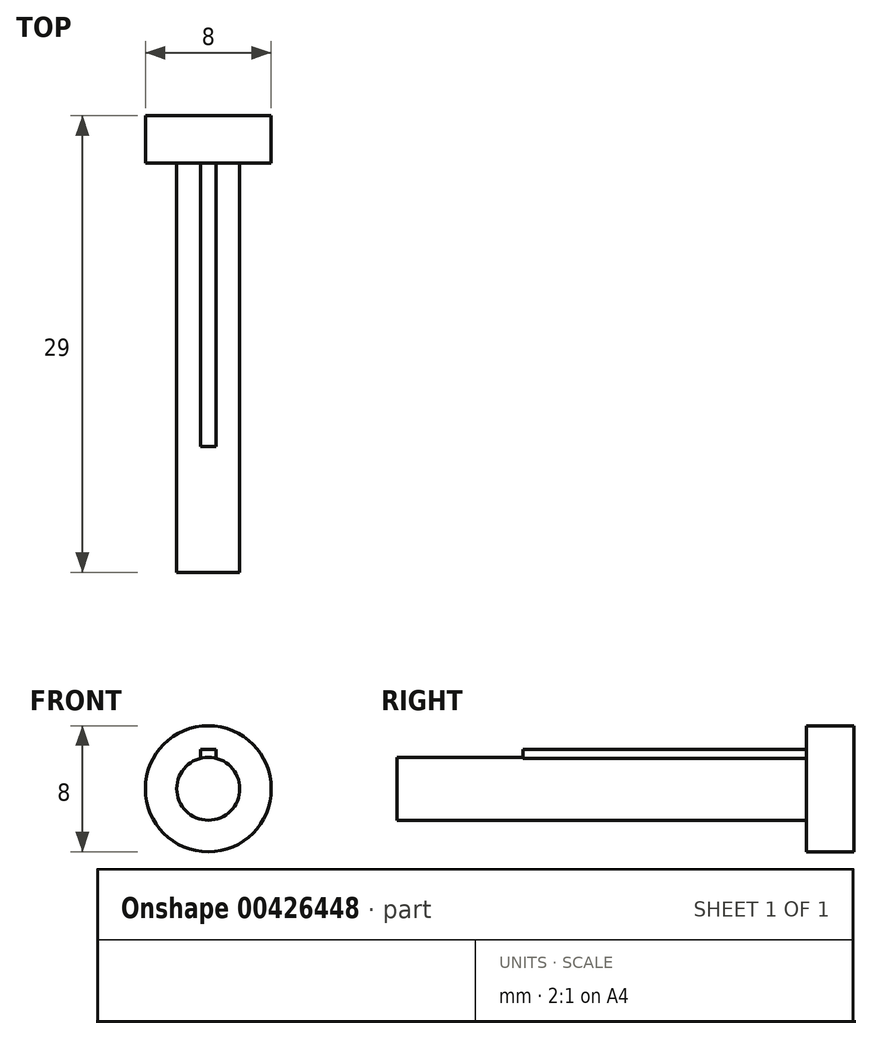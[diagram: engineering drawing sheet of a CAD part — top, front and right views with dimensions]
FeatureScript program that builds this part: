
annotation { "Feature Type Name" : "Feature", "Feature Type Description" : "" }
export const myFeature = defineFeature(function(context is Context, id is Id, definition is map)
    precondition{}
    {
        {
            var Q0;
            Q0=qCreatedBy(makeId("Right.planeOp"),FACE);
            var sketch = newSketch(context, id + "F0", { "sketchPlane" : qUnion([Q0])});
            skLineSegment(sketch, "E0", {"start": v(23.19, 0) * mm, "end": v(23.19, 4) * mm});
            skLineSegment(sketch, "E1", {"start": v(23.19, 4) * mm, "end": v(20.19, 4) * mm});
            skLineSegment(sketch, "E2", {"start": v(20.19, 4) * mm, "end": v(20.19, 2) * mm});
            skLineSegment(sketch, "E3", {"start": v(20.19, 2) * mm, "end": v(-5.81, 2) * mm});
            skLineSegment(sketch, "E4", {"start": v(-5.81, 2) * mm, "end": v(-5.81, 0) * mm});
            skLineSegment(sketch, "E5", {"start": v(-5.81, 0) * mm, "end": v(23.19, 0) * mm});
            skLineSegment(sketch, "E6", {"start": v(-13.83, 0) * mm, "end": v(22.3, 0) * mm, "construction": true});
            skSolve(sketch);
        }
        {
            var Q0;
            Q0 = qSketchRegion(id + "F0", true);
            var Q1;
            Q1=sQuery(id+"F0.wireOp",EDGE,"E6");
            revolve(context, id + "F1", {"entities" : qUnion([Q0]), "axis" : qUnion([Q1]), "revolveType" : RevolveType.FULL});
        }
        {
            var Q0;
            Q0=makeQuery(id+"F1.opRevolve","SWEPT_FACE",FACE,{"disambiguationData":[OSD([sQuery(id+"F0.wireOp",EDGE,"E2")])]});
            var sketch = newSketch(context, id + "F2", { "sketchPlane" : qUnion([Q0])});
            skLineSegment(sketch, "E7.bottom", {"start": v(-0.5, 2.5) * mm, "end": v(0.5, 2.5) * mm});
            skLineSegment(sketch, "E7.top", {"start": v(-0.5, 1.5) * mm, "end": v(0.5, 1.5) * mm});
            skLineSegment(sketch, "E7.left", {"start": v(-0.5, 2.5) * mm, "end": v(-0.5, 1.5) * mm});
            skLineSegment(sketch, "E7.right", {"start": v(0.5, 2.5) * mm, "end": v(0.5, 1.5) * mm});
            skPoint(sketch, "E7.middle", {"position": v(0, 2) * mm});
            skSolve(sketch);
        }
        {
            var Q0;
            Q0 = qSketchRegion(id + "F2", true);
            extrude(context, id + "F3", {"entities" : qUnion([Q0]), "operationType" : NewBodyOperationType.ADD, "depth" : 18 * mm});
        }
    });
